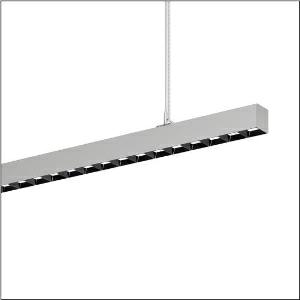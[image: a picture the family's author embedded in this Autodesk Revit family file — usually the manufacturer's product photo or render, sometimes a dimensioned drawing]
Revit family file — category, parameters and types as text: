
# Revit family: silica_r__21_51mx34dc4dsb_5451
name_source: partatom
category: Lighting Fixtures
units: mm (PartAtom-declared; Revit-internal decimal feet)

## family parameters
Cut with Voids When Loaded = No
Host = Face
Light Source = No
Part Type = Normal
Room Calculation Point = No
Round Connector Dimension = Use Diameter
Shared = No

## types (1)
- --- (1 x LED, 19200 lm, 120.3 W, 4000K)
    Apparent Load = 120 VA
    CIE Flux Codes = 74 94 99 56 100
    Color Rendering = 80
    Color Temperature = 4000K
    Default Elevation = 1800 mm
    Description = Silica® 21, office luminaire, primary light control with darklight reflector, of PMMA, black, light emission: direct/indirect distribution, primary light characteristic: asymmetric, installation type: suspended mounting, LED, rated luminous flux: 19.200lm, luminous efficacy: 160lm/W, light colour: 840, colour temperature: 4000K, with terminal, 3+2-pole, max. 2.5mm², mains connection: 220..240V, AC, 50/60Hz, rated input power: 120.3W, luminaire housing, of aluminium, metallic grey (RAL 9006), length: 3.004mm, width: 53mm, height: 53mm, protection rating (complete): IP20, insulation class (complete): insulation class I (protective earthing), certification: CE, permissible operating ambient temperature: 0..+35°C, standard: EN 50419, packaging unit: 1 piece
    Height = 53 mm
    Lamp = 1 x LED
    Lamp Light Flux = 19200 lm
    Lamp Power = 120.3 W
    Lamp count = 1
    Length = 3004 mm
    Luminous efficacy = 160 lm/W
    Manufacturer = Siteco
    ModVariant = No
    Model = 51MX34DC4DSB
    Mounting Place = Ceiling
    Mounting Type = Pendant
    Number of Poles = 1
    OnlyDefault = Yes
    Power Factor = 1
    Product Name = Silica® 21
    Product group = office luminaire | ceiling pendant
    ProductGroupID = 902
    Protection Class = Protection class I
    Protection Degree = IP 20
    RLX_Detail_Level = 1
    RLX_Emergency_Light_Flux = 0 lm
    RLX_Emergency_Type = 0
    RLX_Emergency_Type_DB = No
    RlxData = <blob elided: 66461 chars, md5=105e1e29>
    Socket = socket
    Standby Power = 0 W
    System Light Flux = 19200 lm
    System Power = 120 W
    Type Comments = factory setting: luminous flux: 100 % | dim-lin: 254 | 418 mA
    Type Image = l_1313642.jpg
    URL = http://relux.com
    VarID = @adj_068737
    Voltage = 0 V
    Weight = 0.00 kg
    Width = 53 mm

## geometry (parser evidence)
native form markers: Blend x4, Sweep x12
no freeform markers — native parametric forms only
